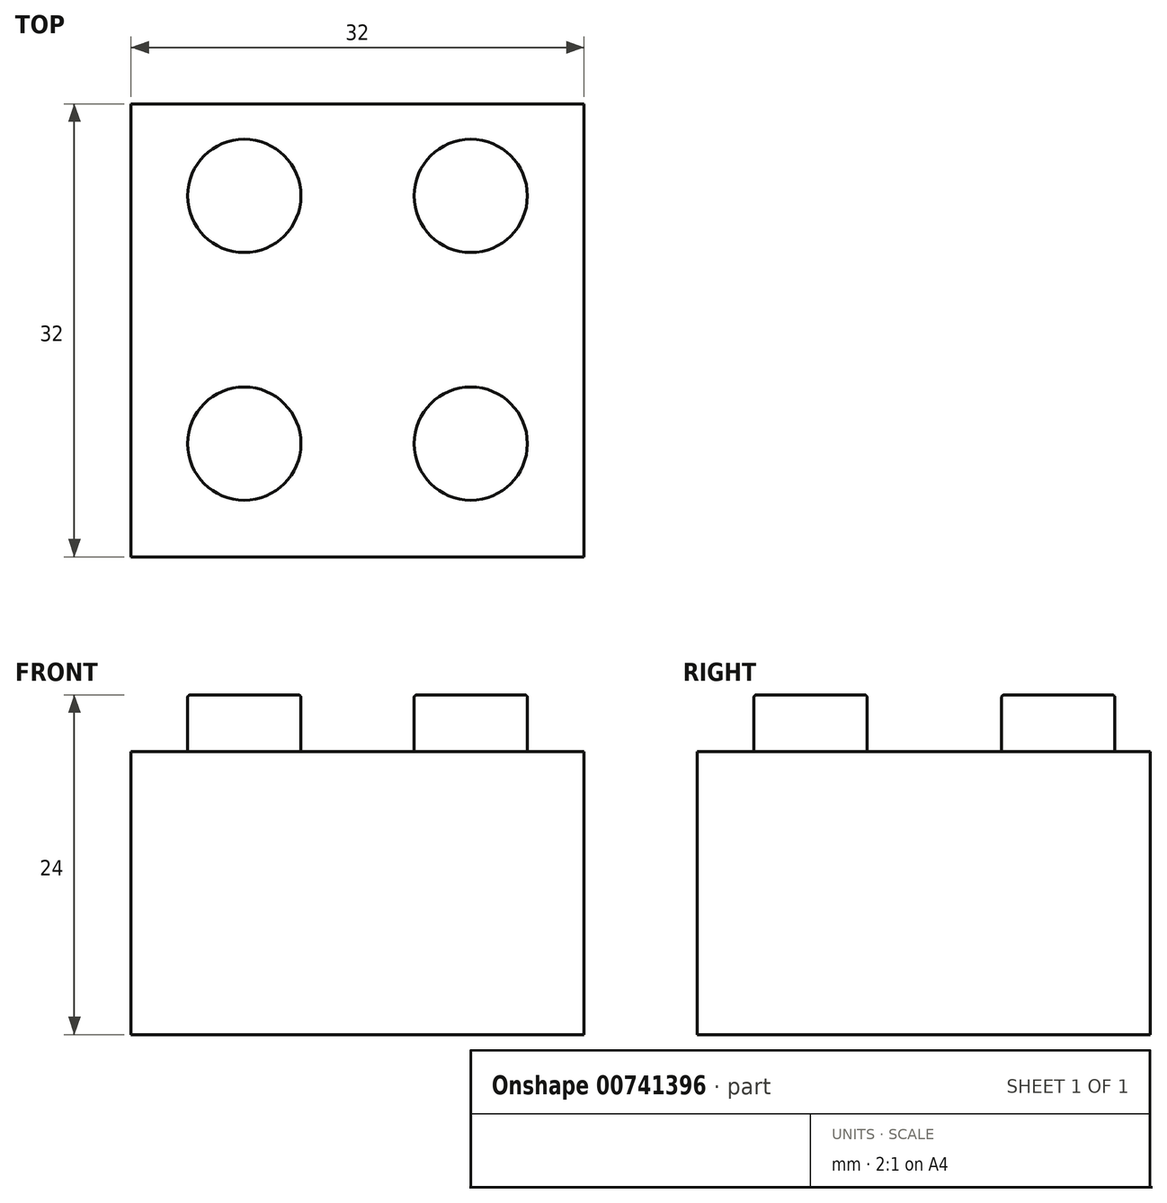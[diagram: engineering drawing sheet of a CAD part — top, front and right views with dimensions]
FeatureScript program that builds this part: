
annotation { "Feature Type Name" : "Feature", "Feature Type Description" : "" }
export const myFeature = defineFeature(function(context is Context, id is Id, definition is map)
    precondition{}
    {
        {
            var Q0;
            Q0=qCreatedBy(makeId("Top.planeOp"),FACE);
            var sketch = newSketch(context, id + "F0", { "sketchPlane" : qUnion([Q0])});
            skLineSegment(sketch, "E0.bottom", {"start": v(4.3, 6.5) * mm, "end": v(36.3, 6.5) * mm});
            skLineSegment(sketch, "E0.top", {"start": v(4.3, -25.5) * mm, "end": v(36.3, -25.5) * mm});
            skLineSegment(sketch, "E0.left", {"start": v(4.3, 6.5) * mm, "end": v(4.3, -25.5) * mm});
            skLineSegment(sketch, "E0.right", {"start": v(36.3, 6.5) * mm, "end": v(36.3, -25.5) * mm});
            skSolve(sketch);
        }
        {
            var Q0;
            Q0=makeQuery(id+"F0.imprint","IMPRINT",FACE,{"disambiguationData":[TD([[makeQuery(id+"F0.imprint","IMPRINT",EDGE,{"derivedFrom":sQuery(id+"F0.wireOp",EDGE,"E0.bottom")}),-1.0]])]});
            extrude(context, id + "F1", {"entities" : qUnion([Q0]), "depth" : 20 * mm, "offsetDistance" : 25 * mm});
        }
        {
            var Q0;
            Q0=makeQuery(id+"F1.opExtrude","CAP_FACE",FACE,{"disambiguationData":[OSD([sQuery(id+"F0.wireOp",EDGE,"E0.bottom"),sQuery(id+"F0.wireOp",EDGE,"E0.top"),sQuery(id+"F0.wireOp",EDGE,"E0.left"),sQuery(id+"F0.wireOp",EDGE,"E0.right")])],"isStart":false});
            var sketch = newSketch(context, id + "F2", { "sketchPlane" : qUnion([Q0])});
            skCircle(sketch, "E1", {"center": v(12.3, 0) * mm, "radius": 4 * mm});
            skSolve(sketch);
        }
        {
            var Q0;
            Q0=makeQuery(id+"F2.imprint","IMPRINT",FACE,{"disambiguationData":[TD([[makeQuery(id+"F2.imprint","IMPRINT",EDGE,{"derivedFrom":sQuery(id+"F2.wireOp",EDGE,"E1")}),1.0]])]});
            extrude(context, id + "F3", {"entities" : qUnion([Q0]), "operationType" : NewBodyOperationType.ADD, "depth" : 4 * mm, "offsetDistance" : 25 * mm});
        }
        {
            var Q0;
            Q0=makeQuery(id+"F1.opExtrude","CAP_FACE",FACE,{"disambiguationData":[OSD([sQuery(id+"F0.wireOp",EDGE,"E0.bottom"),sQuery(id+"F0.wireOp",EDGE,"E0.top"),sQuery(id+"F0.wireOp",EDGE,"E0.left"),sQuery(id+"F0.wireOp",EDGE,"E0.right")])],"isStart":false});
            var sketch = newSketch(context, id + "F4", { "sketchPlane" : qUnion([Q0])});
            skCircle(sketch, "E2", {"center": v(28.3, 0) * mm, "radius": 4 * mm});
            skSolve(sketch);
        }
        {
            var Q0;
            Q0=makeQuery(id+"F4.imprint","IMPRINT",FACE,{"disambiguationData":[TD([[makeQuery(id+"F4.imprint","IMPRINT",EDGE,{"derivedFrom":sQuery(id+"F4.wireOp",EDGE,"E2")}),1.0]])]});
            extrude(context, id + "F5", {"entities" : qUnion([Q0]), "operationType" : NewBodyOperationType.ADD, "depth" : 4 * mm, "offsetDistance" : 25 * mm});
        }
        {
            var Q0;
            Q0=makeQuery(id+"F1.opExtrude","CAP_FACE",FACE,{"disambiguationData":[OSD([sQuery(id+"F0.wireOp",EDGE,"E0.bottom"),sQuery(id+"F0.wireOp",EDGE,"E0.top"),sQuery(id+"F0.wireOp",EDGE,"E0.left"),sQuery(id+"F0.wireOp",EDGE,"E0.right")])],"isStart":false});
            var sketch = newSketch(context, id + "F6", { "sketchPlane" : qUnion([Q0])});
            skSolve(sketch);
        }
        {
            var Q0;
            Q0=makeQuery(id+"F6.imprint","IMPRINT",FACE,{"disambiguationData":[TD([[makeQuery(id+"F6.imprint","IMPRINT",EDGE,{"derivedFrom":makeQuery(id+"F1.opExtrude","CAP_EDGE",EDGE,{"disambiguationData":[OSD([sQuery(id+"F0.wireOp",EDGE,"E0.bottom")])],"isStart":false})}),-1.0]])]});
            var sketch = newSketch(context, id + "F7", { "sketchPlane" : qUnion([Q0])});
            skCircle(sketch, "E3", {"center": v(12.3, -17.5) * mm, "radius": 4 * mm});
            skSolve(sketch);
        }
        {
            var Q0;
            Q0=makeQuery(id+"F7.imprint","IMPRINT",FACE,{"disambiguationData":[TD([[makeQuery(id+"F7.imprint","IMPRINT",EDGE,{"derivedFrom":sQuery(id+"F7.wireOp",EDGE,"E3")}),1.0]])]});
            extrude(context, id + "F8", {"entities" : qUnion([Q0]), "operationType" : NewBodyOperationType.ADD, "depth" : 4 * mm, "offsetDistance" : 25 * mm});
        }
        {
            var Q0;
            Q0=makeQuery(id+"F6.imprint","IMPRINT",FACE,{"disambiguationData":[TD([[makeQuery(id+"F6.imprint","IMPRINT",EDGE,{"derivedFrom":makeQuery(id+"F1.opExtrude","CAP_EDGE",EDGE,{"disambiguationData":[OSD([sQuery(id+"F0.wireOp",EDGE,"E0.bottom")])],"isStart":false})}),-1.0]])]});
            var sketch = newSketch(context, id + "F9", { "sketchPlane" : qUnion([Q0])});
            skSolve(sketch);
        }
        {
            var Q0;
            Q0=makeQuery(id+"F9.imprint","IMPRINT",FACE,{"disambiguationData":[TD([[makeQuery(id+"F9.imprint","IMPRINT",EDGE,{"derivedFrom":makeQuery(id+"F6.imprint","IMPRINT",EDGE,{"derivedFrom":makeQuery(id+"F1.opExtrude","CAP_EDGE",EDGE,{"disambiguationData":[OSD([sQuery(id+"F0.wireOp",EDGE,"E0.bottom")])],"isStart":false})})}),-1.0]])]});
            var sketch = newSketch(context, id + "F10", { "sketchPlane" : qUnion([Q0])});
            skCircle(sketch, "E4", {"center": v(28.3, -17.5) * mm, "radius": 4 * mm});
            skSolve(sketch);
        }
        {
            var Q0;
            Q0=makeQuery(id+"F10.imprint","IMPRINT",FACE,{"disambiguationData":[TD([[makeQuery(id+"F10.imprint","IMPRINT",EDGE,{"derivedFrom":sQuery(id+"F10.wireOp",EDGE,"E4")}),1.0]])]});
            extrude(context, id + "F11", {"entities" : qUnion([Q0]), "operationType" : NewBodyOperationType.ADD, "depth" : 4 * mm, "offsetDistance" : 25 * mm});
        }
        {
            var Q0;
            Q0=makeQuery(id+"F3.opExtrude","CAP_EDGE",EDGE,{"disambiguationData":[OSD([sQuery(id+"F2.wireOp",EDGE,"E1")])],"isStart":false});
            fillet(context, id + "F12", {"entities" : qUnion([Q0]), "radius" : 0.2 * mm, "tangentPropagation" : true, "allowEdgeOverflow" : false});
        }
        {
            var Q0;
            Q0=makeQuery(id+"F8.opExtrude","CAP_EDGE",EDGE,{"disambiguationData":[OSD([sQuery(id+"F7.wireOp",EDGE,"E3")])],"isStart":false});
            fillet(context, id + "F13", {"entities" : qUnion([Q0]), "radius" : 0.2 * mm, "tangentPropagation" : true, "allowEdgeOverflow" : false});
        }
        {
            var Q0;
            Q0=makeQuery(id+"F11.opExtrude","CAP_EDGE",EDGE,{"disambiguationData":[OSD([sQuery(id+"F10.wireOp",EDGE,"E4")])],"isStart":false});
            fillet(context, id + "F14", {"entities" : qUnion([Q0]), "radius" : 0.2 * mm, "tangentPropagation" : true, "allowEdgeOverflow" : false});
        }
        {
            var Q0;
            Q0=makeQuery(id+"F5.opExtrude","CAP_EDGE",EDGE,{"disambiguationData":[OSD([sQuery(id+"F4.wireOp",EDGE,"E2")])],"isStart":false});
            fillet(context, id + "F15", {"entities" : qUnion([Q0]), "radius" : 0.2 * mm, "tangentPropagation" : true, "allowEdgeOverflow" : false});
        }
    });
